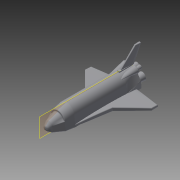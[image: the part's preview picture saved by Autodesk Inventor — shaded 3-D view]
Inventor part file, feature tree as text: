
AUTODESK INVENTOR PART (.ipt)
format: ipt  version: 2015 (Build 190159000, 159)  size: 1,999,360 bytes
history: native  units: in
note: dims shown in document units (in); Inventor stores cm internally (conversion verified against a paired STEP export)
features: sketch x28, plane x14, loft x11, extrude x8, fillet x6, other x3, projected_geometry x3, mirror x2, chamfer x2
ambient origin geometry x8: Origin, YZ Plane, XZ Plane, XY Plane, X Axis, Y Axis, Z Axis, Center Point
bodies: Solid1 (feature_tree)
feature tree (77):
  extrude  "Extrusion1"  TaperAngle=0.0deg  [1 undecoded]
  plane  "Work Plane1"
  plane  "Work Plane2"
  plane  "Work Plane3"
  loft  "Loft1"
  loft  "Loft2"
  fillet  "Fillet1"  Radius=240.6614in
  loft  "Loft4"
  fillet  "Fillet2"  Radius=125.0in
  extrude  "Extrusion2"  TaperAngle=0.0deg  [1 undecoded]
  extrude  "Extrusion3"  Depth=100.0in
  fillet  "Fillet3"  [1 undecoded]
  plane  "Work Plane4"
  mirror  "Mirror1"
  plane  "Work Plane5"
  sketch  "Sketch12"  dims[d36=0.0in d37=90.0deg d38=125.0in]
  loft  "Loft5"
  chamfer  "Chamfer1"  Angle=90.0deg  [1 undecoded]
  chamfer  "Chamfer2"  Angle=90.0deg  [1 undecoded]
  sketch  "Sketch15"  dims[d39=15.0in]
  plane  "Work Plane6"
  plane  "Work Plane7"
  loft  "Loft8"
  mirror  "Mirror2"
  extrude  "Extrusion5"  Depth=125.0in
  extrude  "Extrusion6"  TaperAngle=0.0deg  [1 undecoded]
  plane  "Work Plane8"
  sketch  "Sketch20"  dims[d51=10.0in]
  plane  "Work Plane10"
  loft  "Loft9"
  fillet  "Fillet4"  Radius=84.0in
  extrude  "Extrusion7"  Depth=0.6803in
  fillet  "Fillet5"  Radius=48.0in
  fillet  "Fillet6"  Radius=6500.0in
  sketch  "Sketch23"  dims[d55=0.0in]
  plane  "Work Plane11"
  sketch  "Sketch24"  dims[d56=0.0in]
  loft  "Loft10"
  loft  "Loft11"
  sketch  "Sketch27"  dims[d64=60.0in d70=125.0in]
  plane  "Work Plane12"
  loft  "Loft12"
  loft  "Loft13"
  loft  "Loft14"
  sketch  "Sketch31"  dims[d89=6500.0in d90=7700.0in]
  plane  "Work Plane13"
  sketch  "Sketch32"  dims[d91=10.0in d92=345.0in d93=0.0in]
  sketch  "Sketch33"  dims[d94=10.0in d95=125.0in]
  plane  "Work Plane14"
  extrude  "Extrusion8"  Depth=245.0in
  sketch  "Sketch35"  dims[d98=10.0in d99=0.0in]
  plane  "Work Plane15"
  extrude  "Extrusion9"  Depth=90.0in
  sketch  "Sketch1"  dims[d5=250.0in d12=0.0in]
  sketch  "Sketch2"  dims[d13=75.0in d15=110.0in]
  other  "Edges1"
  sketch  "Sketch3"  dims[d21=98.0in d24=110.0in d25=240.6614in]
  sketch  "Sketch6"  dims[d26=730.0in d27=0.0in d28=300.0in d29=125.0in]
  sketch  "Sketch7"  dims[d30=250.0in d31=0.0in]
  other  "Edges3"
  sketch  "Sketch8"  dims[d32=125.0in d33=100.0in d34=0.0in d35=90.0deg]
  other  "Edges4"
  sketch  "Sketch17"  dims[d40=20.0in]
  sketch  "Sketch18"  dims[d41=10.0in]
  sketch  "Sketch19"  dims[d50=15.0in]
  projected_geometry  "Projected Loop7"
  sketch  "Sketch21"  dims[d52=75.0in]
  sketch  "Sketch22"  dims[d54=125.0in]
  sketch  "Sketch25"  dims[d57=0.0in d58=0.0in d59=90.0deg d60=0.0in d61=90.0deg]
  sketch  "Sketch26"  dims[d62=10.65in d63=50.0in]
  sketch  "Sketch28"  dims[d71=50.0in d72=0.0in d73=90.0deg]
  sketch  "Sketch29"  dims[d74=0.0in d75=90.0deg d76=40.0in d79=84.0in]
  sketch  "Sketch30"  dims[d80=0.0in d82=0.6803in d83=48.0in d84=0.0in d85=6500.0in]
  sketch  "Sketch34"  dims[d96=200.0in d97=0.0in]
  projected_geometry  "Projected Loop8"
  projected_geometry  "Projected Loop9"
  sketch  "Sketch36"  dims[d100=0.0in d101=245.0in d102=90.0in d105=15.0in d106=0.0618in d107=45.0deg d108=345.0in d109=0.0in d110=90.0deg d111=0.0in d112=90.0deg d113=5.2in d114=0.125in d115=45.0deg d116=5.2in d117=0.125in d118=45.0deg d119=-200.0in d126=100.0in d127=25.0in d133=-205.0in d134=50.0in d135=60.0in d137=0.0in d138=90.0deg d139=0.0in d140=90.0deg d141=160.0in d142=100.0in d143=0.6528in d144=0.0in d145=0.0in d146=9000.0in d147=0.0in d148=15.0in d149=25.0in d150=0.0in d151=30.0in d152=0.0in d153=-20.0in d154=30.0in d155=10.0in d156=1.2162in d157=1.2162in d158=195.0in d160=225.0in d166=30.0in d167=225.0in d168=20.0in d169=30.0in d170=20.0in d171=80.0in d172=0.0in d173=90.0deg d174=0.0in d175=90.0deg d176=7.0in d177=0.1374in d178=200.0in d179=0.0in d180=9.475in d184=150.0in d185=150.0in d186=9.475in d187=40.0in d188=80.0in d189=65.0in d190=60.0in d191=20.0in d192=125.0in d193=0.0in d194=13.0in d195=32.0in d196=55.0in d197=55.0in d198=55.0in d199=80.0in d200=95.0in d201=95.0in d202=40.0in d203=0.0in d204=90.0deg d205=0.0in d206=90.0deg d207=0.0in d208=90.0deg d209=0.0in d210=90.0deg d211=25.0in d212=90.0in d213=8.0in d214=0.0in d215=90.0deg d216=0.0in d217=90.0deg d218=105.0in d219=5.0in d220=5.0in d221=0.0in d222=90.0deg d223=0.0in d224=90.0deg d225=105.0in d226=5.0in d227=5.0in d228=0.0in d229=90.0deg d230=0.0in d231=90.0deg d232=-20.0in d233=90.0deg d234=95.0in d235=0.0in d236=90.0deg d237=105.0in d238=0.0in]
note: 6 required parameter values undecoded (feature->parameter linkage not recoverable at this tier; creation-order binding heuristic only, values carry confidence <= 0.55)
